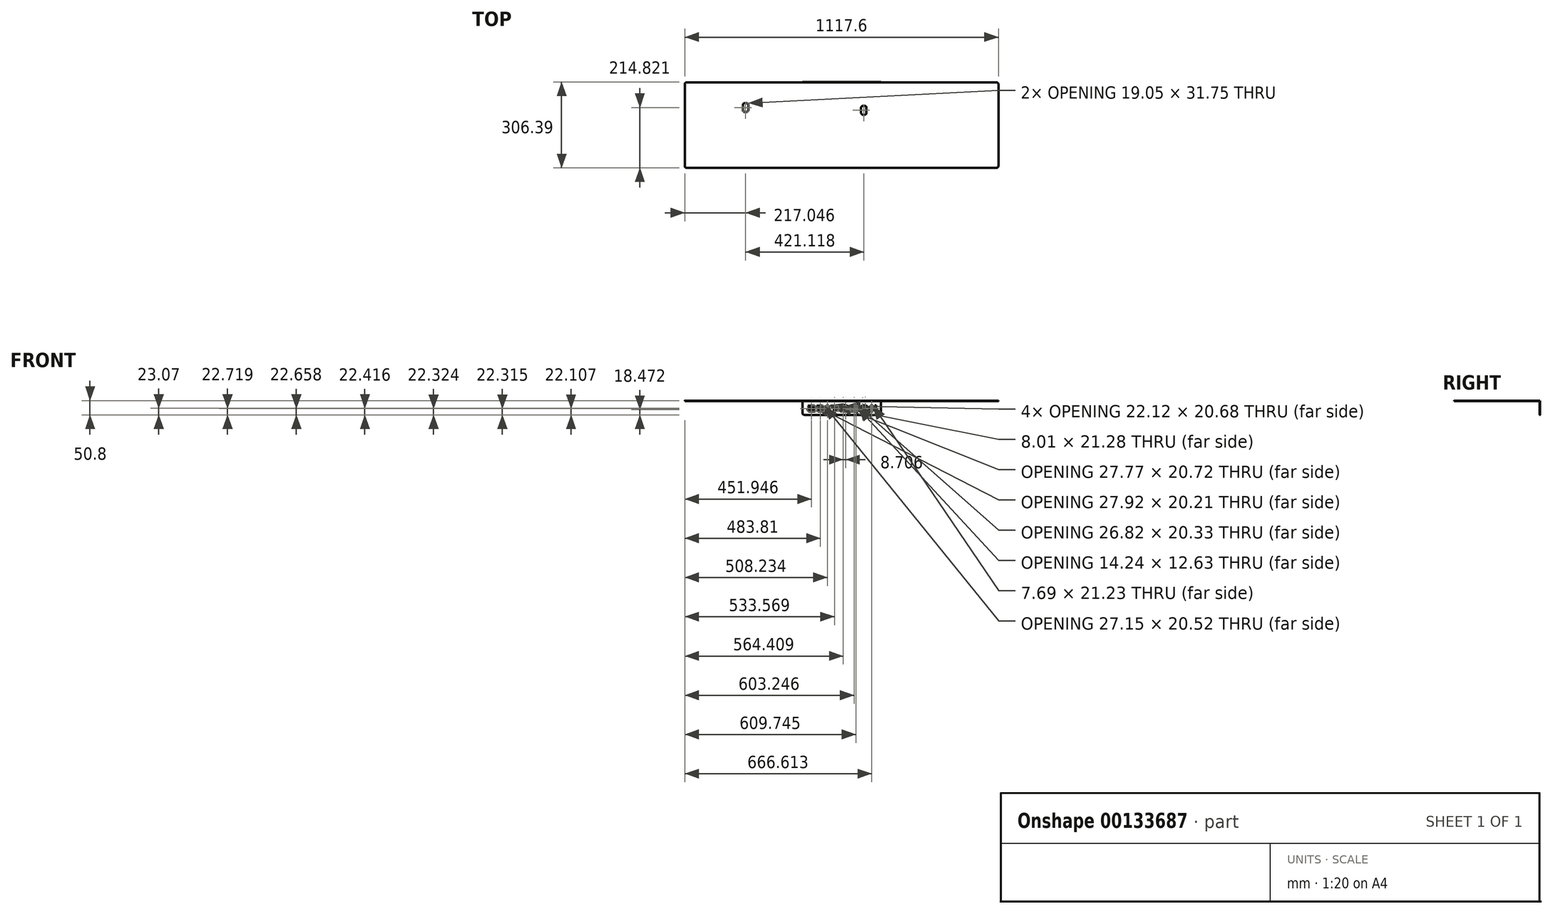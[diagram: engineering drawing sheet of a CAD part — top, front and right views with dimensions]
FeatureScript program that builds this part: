
annotation { "Feature Type Name" : "Feature", "Feature Type Description" : "" }
export const myFeature = defineFeature(function(context is Context, id is Id, definition is map)
    precondition{}
    {
        {
            var Q0;
            Q0=qCreatedBy(makeId("Top.planeOp"),FACE);
            var sketch = newSketch(context, id + "F0", { "sketchPlane" : qUnion([Q0])});
            skLineSegment(sketch, "E0.bottom", {"start": v(558.8, 152.4) * mm, "end": v(-558.8, 152.4) * mm});
            skLineSegment(sketch, "E0.top", {"start": v(558.8, -152.4) * mm, "end": v(-558.8, -152.4) * mm});
            skLineSegment(sketch, "E0.left", {"start": v(558.8, 152.4) * mm, "end": v(558.8, -152.4) * mm});
            skLineSegment(sketch, "E0.right", {"start": v(-558.8, 152.4) * mm, "end": v(-558.8, -152.4) * mm});
            skPoint(sketch, "E0.middle", {"position": v(0, 0) * mm});
            skSolve(sketch);
        }
        {
            var Q0;
            Q0=makeQuery(id+"F0.imprint","IMPRINT",FACE,{"disambiguationData":[TD([[makeQuery(id+"F0.imprint","IMPRINT",EDGE,{"derivedFrom":sQuery(id+"F0.wireOp",EDGE,"E0.bottom")}),1.0]])]});
            extrude(context, id + "F1", {"entities" : qUnion([Q0]), "depth" : 1.59 * mm});
        }
        {
            var Q0;
            Q0=makeQuery(id+"F1.opExtrude","CAP_FACE",FACE,{"disambiguationData":[OSD([sQuery(id+"F0.wireOp",EDGE,"E0.bottom"),sQuery(id+"F0.wireOp",EDGE,"E0.top"),sQuery(id+"F0.wireOp",EDGE,"E0.left"),sQuery(id+"F0.wireOp",EDGE,"E0.right")])],"isStart":false});
            var sketch = newSketch(context, id + "F2", { "sketchPlane" : qUnion([Q0])});
            skLineSegment(sketch, "E1.bottom", {"start": v(506.87, 83) * mm, "end": v(340.87, 83) * mm});
            skLineSegment(sketch, "E1.top", {"start": v(506.87, -83) * mm, "end": v(340.87, -83) * mm});
            skLineSegment(sketch, "E1.left", {"start": v(506.87, 83) * mm, "end": v(506.87, -83) * mm});
            skLineSegment(sketch, "E1.right", {"start": v(340.87, 83) * mm, "end": v(340.87, -83) * mm});
            skPoint(sketch, "E1.middle", {"position": v(423.87, 0) * mm});
            skLineSegment(sketch, "E2.bottom", {"start": v(484.2, 60.33) * mm, "end": v(363.54, 60.33) * mm});
            skLineSegment(sketch, "E2.top", {"start": v(484.2, -60.32) * mm, "end": v(363.54, -60.32) * mm});
            skLineSegment(sketch, "E2.left", {"start": v(484.2, 60.33) * mm, "end": v(484.2, -60.32) * mm});
            skLineSegment(sketch, "E2.right", {"start": v(363.54, 60.33) * mm, "end": v(363.54, -60.32) * mm});
            skLineSegment(sketch, "E3.bottom", {"start": v(290.07, 83) * mm, "end": v(124.07, 83) * mm});
            skLineSegment(sketch, "E3.top", {"start": v(290.07, -83) * mm, "end": v(124.07, -83) * mm});
            skLineSegment(sketch, "E3.left", {"start": v(290.07, 83) * mm, "end": v(290.07, -83) * mm});
            skLineSegment(sketch, "E3.right", {"start": v(124.07, 83) * mm, "end": v(124.07, -83) * mm});
            skPoint(sketch, "E3.middle", {"position": v(207.07, 0) * mm});
            skLineSegment(sketch, "E4.bottom", {"start": v(267.4, 60.32) * mm, "end": v(146.74, 60.32) * mm});
            skLineSegment(sketch, "E4.top", {"start": v(267.4, -60.33) * mm, "end": v(146.74, -60.33) * mm});
            skLineSegment(sketch, "E4.left", {"start": v(267.4, 60.32) * mm, "end": v(267.4, -60.33) * mm});
            skLineSegment(sketch, "E4.right", {"start": v(146.74, 60.32) * mm, "end": v(146.74, -60.33) * mm});
            skLineSegment(sketch, "E5.bottom", {"start": v(34.66, 96.01) * mm, "end": v(-265.06, 96.01) * mm});
            skLineSegment(sketch, "E5.top", {"start": v(34.66, -96.01) * mm, "end": v(-265.06, -96.01) * mm});
            skLineSegment(sketch, "E5.left", {"start": v(34.66, 96.01) * mm, "end": v(34.66, -96.01) * mm});
            skLineSegment(sketch, "E5.right", {"start": v(-265.06, 96.01) * mm, "end": v(-265.06, -96.01) * mm});
            skPoint(sketch, "E5.middle", {"position": v(-115.2, 0) * mm});
            skLineSegment(sketch, "E6.bottom", {"start": v(-418.45, 119.28) * mm, "end": v(-475.6, 119.28) * mm});
            skLineSegment(sketch, "E6.top", {"start": v(-418.45, 30.38) * mm, "end": v(-475.6, 30.38) * mm});
            skLineSegment(sketch, "E6.left", {"start": v(-418.45, 119.28) * mm, "end": v(-418.45, 30.38) * mm});
            skLineSegment(sketch, "E6.right", {"start": v(-475.6, 119.28) * mm, "end": v(-475.6, 30.38) * mm});
            skPoint(sketch, "E6.middle", {"position": v(-447.02, 74.83) * mm});
            skLineSegment(sketch, "E7.bottom", {"start": v(-354.47, -17.8) * mm, "end": v(-506.87, -17.8) * mm});
            skLineSegment(sketch, "E7.top", {"start": v(-354.47, -119.4) * mm, "end": v(-506.87, -119.4) * mm});
            skLineSegment(sketch, "E7.left", {"start": v(-354.47, -17.8) * mm, "end": v(-354.47, -119.4) * mm});
            skLineSegment(sketch, "E7.right", {"start": v(-506.87, -17.8) * mm, "end": v(-506.87, -119.4) * mm});
            skPoint(sketch, "E7.middle", {"position": v(-430.67, -68.6) * mm});
            skLineSegment(sketch, "E8", {"start": v(-506.87, -72.5) * mm, "end": v(-558.8, -72.5) * mm, "construction": true});
            skLineSegment(sketch, "E9", {"start": v(506.87, -7.63) * mm, "end": v(558.8, -7.63) * mm, "construction": true});
            skLineSegment(sketch, "E10", {"start": v(207.07, 83) * mm, "end": v(207.07, 152.4) * mm, "construction": true});
            skLineSegment(sketch, "E11", {"start": v(207.07, -83) * mm, "end": v(207.07, -152.4) * mm, "construction": true});
            skLineSegment(sketch, "E12", {"start": v(-354.47, -68.6) * mm, "end": v(-265.06, -68.6) * mm, "construction": true});
            skLineSegment(sketch, "E13", {"start": v(34.66, -69.65) * mm, "end": v(124.07, -69.65) * mm, "construction": true});
            skSolve(sketch);
        }
        {
            var Q0;
            Q0=makeQuery(id+"F1.opExtrude","CAP_FACE",FACE,{"disambiguationData":[OSD([sQuery(id+"F0.wireOp",EDGE,"E0.bottom"),sQuery(id+"F0.wireOp",EDGE,"E0.top"),sQuery(id+"F0.wireOp",EDGE,"E0.left"),sQuery(id+"F0.wireOp",EDGE,"E0.right")])],"isStart":false});
            var sketch = newSketch(context, id + "F3", { "sketchPlane" : qUnion([Q0])});
            skLineSegment(sketch, "E14.bottom", {"start": v(-338.58, 78.3) * mm, "end": v(-344.93, 78.3) * mm});
            skLineSegment(sketch, "E14.top", {"start": v(-338.58, 46.55) * mm, "end": v(-344.93, 46.55) * mm});
            skLineSegment(sketch, "E14.left", {"start": v(-332.23, 71.95) * mm, "end": v(-332.23, 52.9) * mm});
            skLineSegment(sketch, "E14.right", {"start": v(-351.28, 71.95) * mm, "end": v(-351.28, 52.9) * mm});
            skPoint(sketch, "E14.middle", {"position": v(-341.75, 62.42) * mm});
            skPoint(sketch, "E15.visualSharp", {"position": v(-351.28, 78.3) * mm});
            skArc(sketch, "E15.filletArc", {"start": v(-344.93, 78.3) * mm, "mid": v(-349.42, 76.44) * mm, "end": v(-351.28, 71.95) * mm});
            skPoint(sketch, "E16.visualSharp", {"position": v(-332.23, 78.3) * mm});
            skArc(sketch, "E16.filletArc", {"start": v(-332.23, 71.95) * mm, "mid": v(-334.09, 76.44) * mm, "end": v(-338.58, 78.3) * mm});
            skPoint(sketch, "E17.visualSharp", {"position": v(-332.23, 46.55) * mm});
            skArc(sketch, "E17.filletArc", {"start": v(-338.58, 46.55) * mm, "mid": v(-334.09, 48.4) * mm, "end": v(-332.23, 52.9) * mm});
            skPoint(sketch, "E18.visualSharp", {"position": v(-351.28, 46.55) * mm});
            skArc(sketch, "E18.filletArc", {"start": v(-351.28, 52.9) * mm, "mid": v(-349.42, 48.4) * mm, "end": v(-344.93, 46.55) * mm});
            skLineSegment(sketch, "E19.bottom", {"start": v(82.54, 68.88) * mm, "end": v(76.19, 68.88) * mm});
            skLineSegment(sketch, "E19.top", {"start": v(82.54, 37.13) * mm, "end": v(76.19, 37.13) * mm});
            skLineSegment(sketch, "E19.left", {"start": v(88.89, 62.53) * mm, "end": v(88.89, 43.48) * mm});
            skLineSegment(sketch, "E19.right", {"start": v(69.84, 62.53) * mm, "end": v(69.84, 43.48) * mm});
            skPoint(sketch, "E19.middle", {"position": v(79.36, 53) * mm});
            skPoint(sketch, "E20.visualSharp", {"position": v(69.84, 68.88) * mm});
            skArc(sketch, "E20.filletArc", {"start": v(76.19, 68.88) * mm, "mid": v(71.7, 67.02) * mm, "end": v(69.84, 62.53) * mm});
            skPoint(sketch, "E21.visualSharp", {"position": v(88.89, 68.88) * mm});
            skArc(sketch, "E21.filletArc", {"start": v(88.89, 62.53) * mm, "mid": v(87.03, 67.02) * mm, "end": v(82.54, 68.88) * mm});
            skPoint(sketch, "E22.visualSharp", {"position": v(88.89, 37.13) * mm});
            skArc(sketch, "E22.filletArc", {"start": v(82.54, 37.13) * mm, "mid": v(87.03, 38.98) * mm, "end": v(88.89, 43.48) * mm});
            skPoint(sketch, "E23.visualSharp", {"position": v(69.84, 37.13) * mm});
            skArc(sketch, "E23.filletArc", {"start": v(69.84, 43.48) * mm, "mid": v(71.7, 38.98) * mm, "end": v(76.19, 37.13) * mm});
            skLineSegment(sketch, "E24.0", {"start": v(124.07, 83) * mm, "end": v(124.07, -83) * mm, "construction": true});
            skLineSegment(sketch, "E24.1", {"start": v(34.66, 96.01) * mm, "end": v(34.66, -96.01) * mm, "construction": true});
            skLineSegment(sketch, "E25", {"start": v(69.84, 53) * mm, "end": v(34.66, 53) * mm, "construction": true});
            skLineSegment(sketch, "E26", {"start": v(88.89, 53) * mm, "end": v(124.07, 53) * mm, "construction": true});
            skLineSegment(sketch, "E27.0", {"start": v(-418.45, 119.28) * mm, "end": v(-418.45, 30.38) * mm, "construction": true});
            skLineSegment(sketch, "E27.1", {"start": v(-265.06, 96.01) * mm, "end": v(-265.06, -96.01) * mm, "construction": true});
            skLineSegment(sketch, "E28", {"start": v(-418.45, 65.64) * mm, "end": v(-351.28, 65.64) * mm, "construction": true});
            skLineSegment(sketch, "E29", {"start": v(-332.23, 62.42) * mm, "end": v(-265.06, 62.42) * mm, "construction": true});
            skSolve(sketch);
        }
        {
            var Q0;
            Q0 = qSketchRegion(id + "F3", true);
            var Q1;
            Q1=makeQuery(id+"F1.opExtrude","CAP_FACE",FACE,{"disambiguationData":[OSD([sQuery(id+"F0.wireOp",EDGE,"E0.bottom"),sQuery(id+"F0.wireOp",EDGE,"E0.top"),sQuery(id+"F0.wireOp",EDGE,"E0.left"),sQuery(id+"F0.wireOp",EDGE,"E0.right")])],"isStart":true});
            extrude(context, id + "F4", {"entities" : qUnion([Q0]), "operationType" : NewBodyOperationType.REMOVE, "endBound" : BoundingType.UP_TO_SURFACE, "oppositeDirection" : true, "endBoundEntityFace" : qUnion([Q1]), "depth" : 25.4 * mm});
        }
        {
            var Q0;
            Q0=makeQuery(id+"F1.opExtrude","SWEPT_FACE",FACE,{"disambiguationData":[OSD([sQuery(id+"F0.wireOp",EDGE,"E0.bottom")])]});
            var sketch = newSketch(context, id + "F5", { "sketchPlane" : qUnion([Q0])});
            skLineSegment(sketch, "E30.bottom", {"start": v(139.7, 1.59) * mm, "end": v(-139.7, 1.59) * mm});
            skLineSegment(sketch, "E30.top", {"start": v(139.7, -49.21) * mm, "end": v(-139.7, -49.21) * mm});
            skLineSegment(sketch, "E30.left", {"start": v(139.7, 1.59) * mm, "end": v(139.7, -49.21) * mm});
            skLineSegment(sketch, "E30.right", {"start": v(-139.7, 1.59) * mm, "end": v(-139.7, -49.21) * mm});
            skPoint(sketch, "E30.middle", {"position": v(0, -23.81) * mm});
            skSolve(sketch);
        }
        {
            var Q0;
            Q0 = qSketchRegion(id + "F5", true);
            extrude(context, id + "F6", {"entities" : qUnion([Q0]), "depth" : 1.59 * mm});
        }
        {
            var Q0;
            Q0=makeQuery(id+"F6.opExtrude","CAP_FACE",FACE,{"disambiguationData":[OSD([sQuery(id+"F5.wireOp",EDGE,"E30.bottom"),sQuery(id+"F5.wireOp",EDGE,"E30.top"),sQuery(id+"F5.wireOp",EDGE,"E30.left"),sQuery(id+"F5.wireOp",EDGE,"E30.right")])],"isStart":false});
            var sketch = newSketch(context, id + "F7", { "sketchPlane" : qUnion([Q0])});
            skLineSegment(sketch, "E31", {"start": v(-133.35, -30.21) * mm, "end": v(-139.7, -30.21) * mm, "construction": true});
            skLineSegment(sketch, "E32", {"start": v(133.35, -30.21) * mm, "end": v(139.7, -30.21) * mm, "construction": true});
            skLineSegment(sketch, "E33.bottom", {"start": v(-111.66, -15.52) * mm, "end": v(-103.97, -15.52) * mm});
            skLineSegment(sketch, "E33.top", {"start": v(-111.66, -36.76) * mm, "end": v(-103.97, -36.76) * mm});
            skLineSegment(sketch, "E33.left", {"start": v(-111.66, -15.52) * mm, "end": v(-111.66, -36.76) * mm});
            skLineSegment(sketch, "E33.right", {"start": v(-103.97, -15.52) * mm, "end": v(-103.97, -36.76) * mm});
            skLineSegment(sketch, "E34.bottom", {"start": v(46.56, -15.85) * mm, "end": v(54.57, -15.85) * mm});
            skLineSegment(sketch, "E34.top", {"start": v(46.56, -37.13) * mm, "end": v(54.57, -37.13) * mm});
            skLineSegment(sketch, "E34.left", {"start": v(46.56, -15.85) * mm, "end": v(46.56, -37.13) * mm});
            skLineSegment(sketch, "E34.right", {"start": v(54.57, -15.85) * mm, "end": v(54.57, -37.13) * mm});
            skLineSegment(sketch, "E35", {"start": v(11.35, -21.82) * mm, "end": v(15.62, -16.53) * mm});
            skLineSegment(sketch, "E36", {"start": v(34.85, -21.82) * mm, "end": v(39.12, -16.53) * mm});
            skLineSegment(sketch, "E37", {"start": v(15.62, -16.53) * mm, "end": v(39.12, -16.53) * mm});
            skLineSegment(sketch, "E38", {"start": v(11.35, -21.82) * mm, "end": v(20.67, -21.82) * mm});
            skLineSegment(sketch, "E39.top", {"start": v(20.67, -37.26) * mm, "end": v(27.58, -37.26) * mm});
            skLineSegment(sketch, "E39.left", {"start": v(20.67, -21.82) * mm, "end": v(20.67, -37.26) * mm});
            skLineSegment(sketch, "E39.right", {"start": v(27.58, -21.82) * mm, "end": v(27.58, -37.26) * mm});
            skLineSegment(sketch, "E40.trimOffspring", {"start": v(27.58, -21.82) * mm, "end": v(34.85, -21.82) * mm});
            skArc(sketch, "E41", {"start": v(71.8, -21.51) * mm, "mid": v(68.1, -26.55) * mm, "end": v(72.07, -31.36) * mm});
            skLineSegment(sketch, "E42", {"start": v(83.85, -21.51) * mm, "end": v(88.07, -16.3) * mm});
            skLineSegment(sketch, "E43", {"start": v(88.56, -31.36) * mm, "end": v(84.17, -36.8) * mm});
            skLineSegment(sketch, "E44", {"start": v(72.07, -31.36) * mm, "end": v(88.56, -31.36) * mm});
            skLineSegment(sketch, "E45", {"start": v(83.85, -21.51) * mm, "end": v(71.8, -21.51) * mm});
            skArc(sketch, "E46", {"start": v(69.89, -16.3) * mm, "mid": v(61.41, -26.28) * mm, "end": v(69.2, -36.8) * mm});
            skLineSegment(sketch, "E47", {"start": v(69.2, -36.8) * mm, "end": v(84.17, -36.8) * mm});
            skLineSegment(sketch, "E48", {"start": v(69.89, -16.3) * mm, "end": v(88.07, -16.3) * mm});
            skLineSegment(sketch, "E49", {"start": v(116.3, -21.93) * mm, "end": v(120.53, -16.7) * mm});
            skLineSegment(sketch, "E50", {"start": v(92.9, -36.9) * mm, "end": v(96.83, -32.03) * mm});
            skArc(sketch, "E51", {"start": v(100.44, -21.93) * mm, "mid": v(99.82, -23.31) * mm, "end": v(100.59, -24.62) * mm});
            skArc(sketch, "E52", {"start": v(113.8, -32.03) * mm, "mid": v(114.68, -30.42) * mm, "end": v(113.68, -28.9) * mm});
            skArc(sketch, "E53", {"start": v(98, -16.7) * mm, "mid": v(93.45, -22.82) * mm, "end": v(98.07, -28.9) * mm});
            skArc(sketch, "E54", {"start": v(116.53, -36.9) * mm, "mid": v(120.81, -30.95) * mm, "end": v(117.12, -24.62) * mm});
            skLineSegment(sketch, "E55", {"start": v(98, -16.7) * mm, "end": v(120.53, -16.7) * mm});
            skLineSegment(sketch, "E56", {"start": v(98.07, -28.9) * mm, "end": v(113.68, -28.9) * mm});
            skLineSegment(sketch, "E57", {"start": v(100.44, -21.93) * mm, "end": v(116.3, -21.93) * mm});
            skLineSegment(sketch, "E58", {"start": v(100.59, -24.62) * mm, "end": v(117.12, -24.62) * mm});
            skLineSegment(sketch, "E59", {"start": v(92.9, -36.9) * mm, "end": v(116.53, -36.9) * mm});
            skLineSegment(sketch, "E60", {"start": v(96.83, -32.03) * mm, "end": v(113.8, -32.03) * mm});
            skLineSegment(sketch, "E61", {"start": v(-123.43, -15.9) * mm, "end": v(-118.39, -15.9) * mm});
            skLineSegment(sketch, "E62", {"start": v(-122.04, -24.2) * mm, "end": v(-119.77, -24.2) * mm});
            skLineSegment(sketch, "E63", {"start": v(-123.43, -15.9) * mm, "end": v(-122.04, -24.2) * mm});
            skLineSegment(sketch, "E64", {"start": v(-118.39, -15.9) * mm, "end": v(-119.77, -24.2) * mm});
            skEllipticalArc(sketch, "E65", {});
            skEllipticalArc(sketch, "E66", {});
            skEllipticalArc(sketch, "E67", {});
            skEllipticalArc(sketch, "E68", {});
            skLineSegment(sketch, "E69", {"start": v(-80.51, -20.89) * mm, "end": v(-80.51, -32.83) * mm, "construction": true});
            skLineSegment(sketch, "E70", {"start": v(-89, -26.86) * mm, "end": v(-72.04, -26.86) * mm, "construction": true});
            skLineSegment(sketch, "E71", {"start": v(-84.7, -32.05) * mm, "end": v(-80.51, -26.86) * mm, "construction": true});
            skLineSegment(sketch, "E72", {"start": v(-80.51, -26.86) * mm, "end": v(-76.32, -21.67) * mm, "construction": true});
            skLineSegment(sketch, "E73", {"start": v(-77.62, -21.25) * mm, "end": v(-73.8, -16.53) * mm});
            skLineSegment(sketch, "E74", {"start": v(-75.15, -22.24) * mm, "end": v(-71.39, -17.58) * mm});
            skLineSegment(sketch, "E75", {"start": v(-76.32, -21.67) * mm, "end": v(-72.57, -17.02) * mm, "construction": true});
            skLineSegment(sketch, "E76", {"start": v(-76.22, -19.52) * mm, "end": v(-75.23, -20.32) * mm});
            skLineSegment(sketch, "E77", {"start": v(-75.23, -20.32) * mm, "end": v(-74.24, -21.12) * mm});
            skLineSegment(sketch, "E78", {"start": v(-84.7, -32.05) * mm, "end": v(-88.46, -36.7) * mm, "construction": true});
            skLineSegment(sketch, "E79", {"start": v(-85.88, -31.48) * mm, "end": v(-89.64, -36.13) * mm});
            skLineSegment(sketch, "E80", {"start": v(-83.41, -32.47) * mm, "end": v(-87.22, -37.18) * mm});
            skLineSegment(sketch, "E81", {"start": v(-87.35, -33.3) * mm, "end": v(-86.36, -34.1) * mm, "construction": true});
            skLineSegment(sketch, "E82", {"start": v(-86.36, -34.1) * mm, "end": v(-85.34, -34.86) * mm, "construction": true});
            skLineSegment(sketch, "E83", {"start": v(-18.44, -26.04) * mm, "end": v(-1.49, -26.04) * mm, "construction": true});
            skLineSegment(sketch, "E84", {"start": v(-9.96, -20.07) * mm, "end": v(-9.96, -32.01) * mm, "construction": true});
            skLineSegment(sketch, "E85", {"start": v(-9.96, -26.04) * mm, "end": v(-5.77, -20.85) * mm, "construction": true});
            skLineSegment(sketch, "E86", {"start": v(-9.96, -26.04) * mm, "end": v(-14.15, -31.23) * mm, "construction": true});
            skLineSegment(sketch, "E87", {"start": v(-5.77, -20.85) * mm, "end": v(-2.01, -16.2) * mm, "construction": true});
            skLineSegment(sketch, "E88", {"start": v(-14.15, -31.23) * mm, "end": v(-17.91, -35.88) * mm, "construction": true});
            skLineSegment(sketch, "E89", {"start": v(-7.06, -20.43) * mm, "end": v(-3.26, -15.72) * mm});
            skLineSegment(sketch, "E90", {"start": v(-4.6, -21.42) * mm, "end": v(-0.84, -16.77) * mm});
            skLineSegment(sketch, "E91", {"start": v(-5.16, -18.08) * mm, "end": v(-4.17, -18.87) * mm, "construction": true});
            skLineSegment(sketch, "E92", {"start": v(-4.17, -18.87) * mm, "end": v(-3.18, -19.67) * mm, "construction": true});
            skLineSegment(sketch, "E93", {"start": v(-15.33, -30.66) * mm, "end": v(-19.09, -35.32) * mm});
            skLineSegment(sketch, "E94", {"start": v(-12.86, -31.65) * mm, "end": v(-16.67, -36.37) * mm});
            skLineSegment(sketch, "E95", {"start": v(-16.13, -33.67) * mm, "end": v(-17.11, -32.87) * mm, "construction": true});
            skLineSegment(sketch, "E96", {"start": v(-16.13, -33.67) * mm, "end": v(-15.14, -34.47) * mm, "construction": true});
            skEllipticalArc(sketch, "E97.trimOffspring", {});
            skEllipticalArc(sketch, "E98.trimOffspring", {});
            skEllipticalArc(sketch, "E99.trimOffspring", {});
            skEllipticalArc(sketch, "E100.trimOffspring", {});
            skLineSegment(sketch, "E101.bottom", {"start": v(-58.07, -24.42) * mm, "end": v(-43.82, -24.42) * mm});
            skLineSegment(sketch, "E101.top", {"start": v(-58.07, -37.05) * mm, "end": v(-54.03, -37.05) * mm});
            skLineSegment(sketch, "E101.left", {"start": v(-58.07, -24.42) * mm, "end": v(-58.07, -37.05) * mm});
            skLineSegment(sketch, "E102.bottom", {"start": v(-52.9, -29.08) * mm, "end": v(-47.59, -29.08) * mm});
            skLineSegment(sketch, "E102.top", {"start": v(-52.9, -32.62) * mm, "end": v(-50.45, -32.62) * mm});
            skLineSegment(sketch, "E102.left", {"start": v(-52.9, -29.08) * mm, "end": v(-52.9, -32.62) * mm});
            skArc(sketch, "E103", {"start": v(-39, -32.62) * mm, "mid": v(-37.8, -30.85) * mm, "end": v(-39, -29.08) * mm});
            skLineSegment(sketch, "E104.bottom", {"start": v(-57.85, -21.51) * mm, "end": v(-38.9, -21.51) * mm});
            skLineSegment(sketch, "E104.top", {"start": v(-53.98, -16.72) * mm, "end": v(-35.46, -16.72) * mm});
            skLineSegment(sketch, "E105", {"start": v(-57.85, -21.51) * mm, "end": v(-53.98, -16.72) * mm});
            skArc(sketch, "E106", {"start": v(-38.9, -24.42) * mm, "mid": v(-37.69, -22.97) * mm, "end": v(-38.9, -21.51) * mm});
            skArc(sketch, "E107", {"start": v(-35.46, -26.65) * mm, "mid": v(-31.49, -21.69) * mm, "end": v(-35.46, -16.72) * mm});
            skLineSegment(sketch, "E108", {"start": v(-35.46, -37.05) * mm, "end": v(-38.9, -37.05) * mm});
            skArc(sketch, "E109", {"start": v(-35.46, -37.05) * mm, "mid": v(-31.04, -31.85) * mm, "end": v(-35.46, -26.65) * mm});
            skLineSegment(sketch, "E110", {"start": v(-39, -29.08) * mm, "end": v(-39, -32.62) * mm});
            skLineSegment(sketch, "E111", {"start": v(-52.9, -30.85) * mm, "end": v(-39, -30.85) * mm, "construction": true});
            skLineSegment(sketch, "E112", {"start": v(-45.95, -29.08) * mm, "end": v(-45.95, -32.62) * mm, "construction": true});
            skLineSegment(sketch, "E113", {"start": v(-47.59, -29.08) * mm, "end": v(-43.82, -24.42) * mm});
            skLineSegment(sketch, "E114", {"start": v(-44.32, -29.08) * mm, "end": v(-40.56, -24.42) * mm});
            skLineSegment(sketch, "E115", {"start": v(-45.95, -29.08) * mm, "end": v(-42.2, -24.42) * mm, "construction": true});
            skLineSegment(sketch, "E116", {"start": v(-44.22, -26.94) * mm, "end": v(-43.24, -27.74) * mm, "construction": true});
            skLineSegment(sketch, "E117", {"start": v(-44.22, -26.94) * mm, "end": v(-45.21, -26.14) * mm, "construction": true});
            skLineSegment(sketch, "E118.trimOffspring", {"start": v(-47.18, -32.62) * mm, "end": v(-39, -32.62) * mm});
            skLineSegment(sketch, "E119.trimOffspring", {"start": v(-50.76, -37.05) * mm, "end": v(-38.9, -37.05) * mm});
            skLineSegment(sketch, "E120.trimOffspring", {"start": v(-44.32, -29.08) * mm, "end": v(-39, -29.08) * mm});
            skLineSegment(sketch, "E121.trimOffspring", {"start": v(-40.56, -24.42) * mm, "end": v(-38.9, -24.42) * mm});
            skLineSegment(sketch, "E122.trimOffspring", {"start": v(-50.45, -32.62) * mm, "end": v(-54.03, -37.05) * mm});
            skLineSegment(sketch, "E123.trimOffspring", {"start": v(-47.18, -32.62) * mm, "end": v(-50.76, -37.05) * mm});
            const initialGuessF7  = {"E65": [-0.08051430433988571, -0.026858070865273476, 1, 0, 0.00847725, 0.005969, 4.363346940728332, 0.8854703331738099], "E66": [-0.08051430433988571, -0.026858070865273476, 1, 0, 0.015621, 0.01143, 4.2686185518055435, 0.9468935535916937], "E67": [-0.009962615557014942, -0.0260420273989439, 1, 0, 0.00847725, 0.005969, 4.363447628581776, 0.8854703331738103], "E68": [-0.009962615557014942, -0.0260420273989439, 1, 0, 0.015621, 0.01143, 4.268672121506316, 0.9468935535916986], "E97.trimOffspring": [-0.08051430433988571, -0.026858070865273476, 1, 0, 0.00847725, 0.005969, 1.2218549749919867, 4.0270629867636005], "E98.trimOffspring": [-0.08051430433988571, -0.026858070865273476, 1, 0, 0.015621, 0.01143, 1.127079467916527, 4.088486207181484], "E99.trimOffspring": [-0.009962615557014942, -0.0260420273989439, 1, 0, 0.00847725, 0.005969, 1.2218549749919836, 4.0270629867636085], "E100.trimOffspring": [-0.009962615557014942, -0.0260420273989439, 1, 0, 0.015621, 0.01143, 1.1270794679165246, 4.088486207181486]};
            skSetInitialGuess(sketch, initialGuessF7);
            skSolve(sketch);
        }
        {
            var Q0;
            Q0 = qSketchRegion(id + "F7", true);
            var Q1;
            Q1=makeQuery(id+"F6.opExtrude","CAP_FACE",FACE,{"disambiguationData":[OSD([sQuery(id+"F5.wireOp",EDGE,"E30.bottom"),sQuery(id+"F5.wireOp",EDGE,"E30.top"),sQuery(id+"F5.wireOp",EDGE,"E30.left"),sQuery(id+"F5.wireOp",EDGE,"E30.right")])],"isStart":true});
            extrude(context, id + "F8", {"entities" : qUnion([Q0]), "operationType" : NewBodyOperationType.REMOVE, "endBound" : BoundingType.UP_TO_SURFACE, "oppositeDirection" : true, "endBoundEntityFace" : qUnion([Q1]), "depth" : 25.4 * mm});
        }
        {
            var Q0;
            Q0=makeQuery(id+"F1.opExtrude","SWEPT_EDGE",EDGE,{"disambiguationData":[OSD([sQuery(id+"F0.wireOp",EDGE,"E0.bottom"),sQuery(id+"F0.wireOp",EDGE,"E0.right")])]});
            var Q1;
            Q1=makeQuery(id+"F1.opExtrude","SWEPT_EDGE",EDGE,{"disambiguationData":[OSD([sQuery(id+"F0.wireOp",EDGE,"E0.top"),sQuery(id+"F0.wireOp",EDGE,"E0.right")])]});
            var Q2;
            Q2=makeQuery(id+"F1.opExtrude","SWEPT_EDGE",EDGE,{"disambiguationData":[OSD([sQuery(id+"F0.wireOp",EDGE,"E0.top"),sQuery(id+"F0.wireOp",EDGE,"E0.left")])]});
            var Q3;
            Q3=makeQuery(id+"F1.opExtrude","SWEPT_EDGE",EDGE,{"disambiguationData":[OSD([sQuery(id+"F0.wireOp",EDGE,"E0.bottom"),sQuery(id+"F0.wireOp",EDGE,"E0.left")])]});
            fillet(context, id + "F9", {"entities" : qUnion([Q0, Q1, Q2, Q3]), "radius" : 6.35 * mm, "tangentPropagation" : true, "allowEdgeOverflow" : false});
        }
        {
            var Q0;
            Q0=makeQuery(id+"F6.opExtrude","SWEPT_EDGE",EDGE,{"disambiguationData":[OSD([sQuery(id+"F5.wireOp",EDGE,"E30.top"),sQuery(id+"F5.wireOp",EDGE,"E30.left")])]});
            var Q1;
            Q1=makeQuery(id+"F6.opExtrude","SWEPT_EDGE",EDGE,{"disambiguationData":[OSD([sQuery(id+"F5.wireOp",EDGE,"E30.top"),sQuery(id+"F5.wireOp",EDGE,"E30.right")])]});
            fillet(context, id + "F10", {"entities" : qUnion([Q0, Q1]), "radius" : 6.35 * mm, "tangentPropagation" : true, "allowEdgeOverflow" : false});
        }
    });
